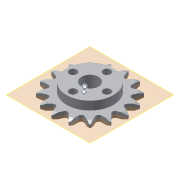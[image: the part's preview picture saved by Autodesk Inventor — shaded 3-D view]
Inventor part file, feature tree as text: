
AUTODESK INVENTOR PART (.ipt)
format: ipt  version: 2013 (Build 170138000, 138)  size: 419,840 bytes
history: native  units: in
note: dims shown in document units (in); Inventor stores cm internally (conversion verified against a paired STEP export)
features: other x17, plane x1
ambient origin geometry x8: Origin, YZ Plane, XZ Plane, XY Plane, X Axis, Y Axis, Z Axis, Center Point
bodies: Solid1 (feature_tree)
feature tree (18):
  other  "Tetrix sprocket 16T.ipt"
  other  "sprocket_25_16t_tetrix::Tetrix sprocket 16T.ipt"
  other  "TaggingFeature1"
  other  "FRONT"
  other  "TOP"
  other  "RIGHT"
  plane  "Work Plane4"
  other  "A_1"
  other  "A_2"
  other  "A_4"
  other  "A_5"
  other  "A_6"
  other  "A_3"
  other  "A_7"
  other  "A_8"
  other  "A_9"
  other  "iComposite:2"
  other  "iComposite:1"
